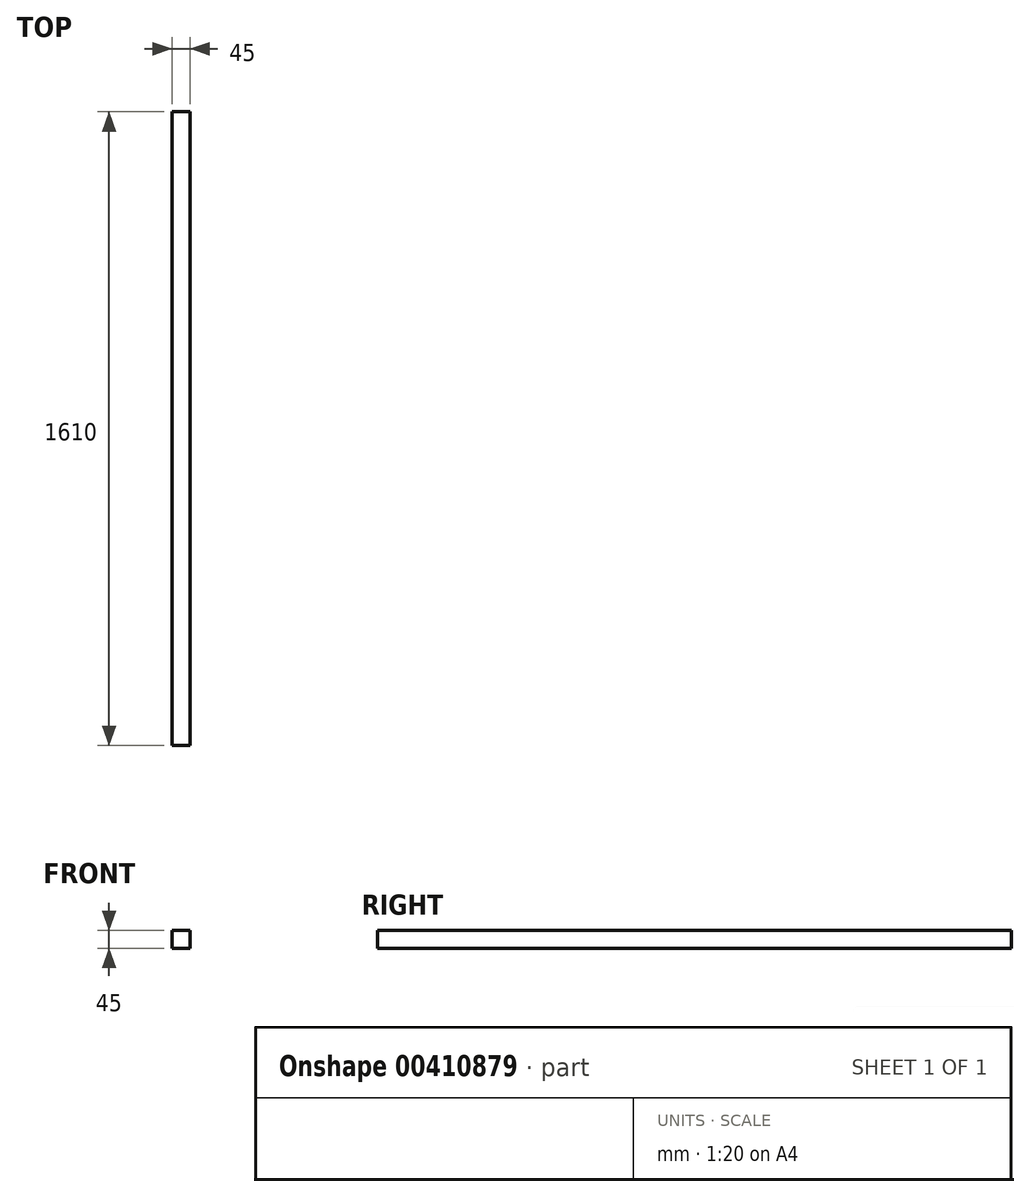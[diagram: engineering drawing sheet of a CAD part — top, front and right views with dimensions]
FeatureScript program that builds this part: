
annotation { "Feature Type Name" : "Feature", "Feature Type Description" : "" }
export const myFeature = defineFeature(function(context is Context, id is Id, definition is map)
    precondition{}
    {
        {
            var Q0;
            Q0=qCreatedBy(makeId("Top.planeOp"),FACE);
            var sketch = newSketch(context, id + "F0", { "sketchPlane" : qUnion([Q0])});
            skLineSegment(sketch, "E0.bottom", {"start": v(62.34, -811.7) * mm, "end": v(107.34, -811.7) * mm});
            skLineSegment(sketch, "E0.top", {"start": v(62.34, 798.3) * mm, "end": v(107.34, 798.3) * mm});
            skLineSegment(sketch, "E0.left", {"start": v(62.34, -811.7) * mm, "end": v(62.34, 798.3) * mm});
            skLineSegment(sketch, "E0.right", {"start": v(107.34, -811.7) * mm, "end": v(107.34, 798.3) * mm});
            skSolve(sketch);
        }
        {
            var Q0;
            Q0 = qSketchRegion(id + "F0", true);
            extrude(context, id + "F1", {"entities" : qUnion([Q0]), "depth" : 45 * mm});
        }
    });
